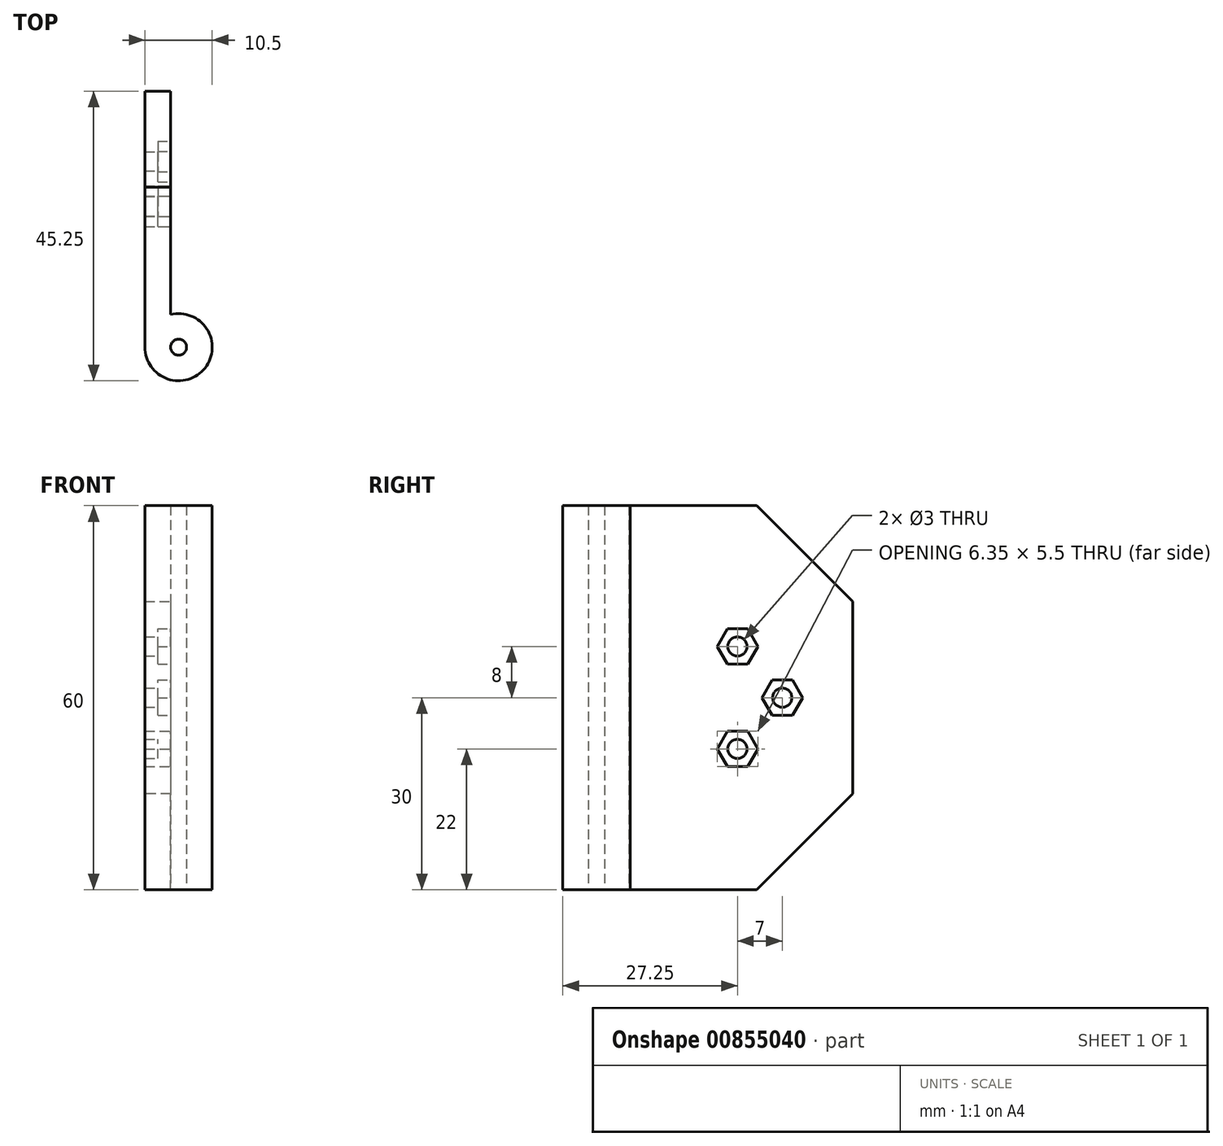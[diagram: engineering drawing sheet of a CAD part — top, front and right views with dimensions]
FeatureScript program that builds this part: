
annotation { "Feature Type Name" : "Feature", "Feature Type Description" : "" }
export const myFeature = defineFeature(function(context is Context, id is Id, definition is map)
    precondition{}
    {
        {
            var Q0;
            Q0=qCreatedBy(makeId("Top.planeOp"),FACE);
            var sketch = newSketch(context, id + "F0", { "sketchPlane" : qUnion([Q0])});
            skCircle(sketch, "E0", {"center": v(0, 0) * mm, "radius": 1.25 * mm});
            skCircle(sketch, "E1.0", {"center": v(0, 0) * mm, "radius": 5.25 * mm});
            skLineSegment(sketch, "E2", {"start": v(-5.25, 0) * mm, "end": v(-5.25, 40) * mm});
            skLineSegment(sketch, "E3", {"start": v(-5.25, 40) * mm, "end": v(-1.25, 40) * mm});
            skLineSegment(sketch, "E4", {"start": v(-1.25, 40) * mm, "end": v(-1.25, 0) * mm});
            skSolve(sketch);
        }
        {
            var Q0;
            {var subQ0=sQuery(id+"F0.wireOp",EDGE,"E2");Q0=makeQuery(id+"F0.imprint","IMPRINT",FACE,{"disambiguationData":[TD([[makeQuery(id+"F0.imprint","IMPRINT",EDGE,{"derivedFrom":subQ0}),-1.0]])]});}
            var Q1;
            Q1=makeQuery(id+"F0.imprint","IMPRINT",FACE,{"disambiguationData":[TD([[makeQuery(id+"F0.imprint","IMPRINT",EDGE,{"derivedFrom":sQuery(id+"F0.wireOp",EDGE,"E0")}),-1.0]])]});
            extrude(context, id + "F1", {"entities" : qUnion([Q0, Q1]), "endBound" : BoundingType.SYMMETRIC, "depth" : 60 * mm, "offsetDistance" : 25 * mm});
        }
        {
            var Q0;
            Q0=makeQuery(id+"F1.opExtrude","SWEPT_FACE",FACE,{"disambiguationData":[OSD([sQuery(id+"F0.wireOp",EDGE,"E4")])]});
            var sketch = newSketch(context, id + "F2", { "sketchPlane" : qUnion([Q0])});
            skLineSegment(sketch, "E5", {"start": v(0, 0) * mm, "end": v(29, 0) * mm, "construction": true});
            skLineSegment(sketch, "E6", {"start": v(22, 0) * mm, "end": v(22, 8) * mm, "construction": true});
            skPoint(sketch, "E7", {"position": v(22, 0) * mm});
            skCircle(sketch, "E8", {"center": v(22, 8) * mm, "radius": 1.5 * mm});
            skCircle(sketch, "E9", {"center": v(29, 0) * mm, "radius": 1.5 * mm});
            skCircle(sketch, "E10.MirrorC", {"center": v(22, -8) * mm, "radius": 1.5 * mm});
            skCircle(sketch, "E11.cCircle", {"center": v(22, 8) * mm, "radius": 2.75 * mm, "construction": true});
            skLineSegment(sketch, "E11.0", {"start": v(20.41, 10.75) * mm, "end": v(23.59, 10.75) * mm});
            skLineSegment(sketch, "E11.1", {"start": v(23.59, 10.75) * mm, "end": v(25.18, 8) * mm});
            skLineSegment(sketch, "E11.2", {"start": v(25.18, 8) * mm, "end": v(23.59, 5.25) * mm});
            skLineSegment(sketch, "E11.3", {"start": v(23.59, 5.25) * mm, "end": v(20.41, 5.25) * mm});
            skLineSegment(sketch, "E11.4", {"start": v(20.41, 5.25) * mm, "end": v(18.82, 8) * mm});
            skLineSegment(sketch, "E11.5", {"start": v(18.82, 8) * mm, "end": v(20.41, 10.75) * mm});
            skPoint(sketch, "E11.0.midPoint", {"position": v(22, 10.75) * mm});
            skCircle(sketch, "E12.MirrorC", {"center": v(22, -8) * mm, "radius": 2.75 * mm, "construction": true});
            skLineSegment(sketch, "E13.MirrorCS", {"start": v(20.41, -5.25) * mm, "end": v(18.82, -8) * mm});
            skLineSegment(sketch, "E14.MirrorCS", {"start": v(23.59, -5.25) * mm, "end": v(20.41, -5.25) * mm});
            skLineSegment(sketch, "E15.MirrorCS", {"start": v(25.18, -8) * mm, "end": v(23.59, -5.25) * mm});
            skLineSegment(sketch, "E16.MirrorCS", {"start": v(23.59, -10.75) * mm, "end": v(25.18, -8) * mm});
            skLineSegment(sketch, "E17.MirrorCS", {"start": v(20.41, -10.75) * mm, "end": v(23.59, -10.75) * mm});
            skLineSegment(sketch, "E18.MirrorCS", {"start": v(18.82, -8) * mm, "end": v(20.41, -10.75) * mm});
            skCircle(sketch, "E19.cCircle", {"center": v(29, 0) * mm, "radius": 2.75 * mm, "construction": true});
            skLineSegment(sketch, "E19.0", {"start": v(27.41, 2.75) * mm, "end": v(30.59, 2.75) * mm});
            skLineSegment(sketch, "E19.1", {"start": v(30.59, 2.75) * mm, "end": v(32.18, 0) * mm});
            skLineSegment(sketch, "E19.2", {"start": v(32.18, 0) * mm, "end": v(30.59, -2.75) * mm});
            skLineSegment(sketch, "E19.3", {"start": v(30.59, -2.75) * mm, "end": v(27.41, -2.75) * mm});
            skLineSegment(sketch, "E19.4", {"start": v(27.41, -2.75) * mm, "end": v(25.82, 0) * mm});
            skLineSegment(sketch, "E19.5", {"start": v(25.82, 0) * mm, "end": v(27.41, 2.75) * mm});
            skPoint(sketch, "E19.0.midPoint", {"position": v(29, 2.75) * mm});
            skSolve(sketch);
        }
        {
            var Q0;
            Q0=makeQuery(id+"F2.imprint","IMPRINT",FACE,{"disambiguationData":[TD([[makeQuery(id+"F2.imprint","IMPRINT",EDGE,{"derivedFrom":sQuery(id+"F2.wireOp",EDGE,"E8")}),1.0]])]});
            var Q1;
            Q1=makeQuery(id+"F2.imprint","IMPRINT",FACE,{"disambiguationData":[TD([[makeQuery(id+"F2.imprint","IMPRINT",EDGE,{"derivedFrom":sQuery(id+"F2.wireOp",EDGE,"E9")}),1.0]])]});
            var Q2;
            Q2=makeQuery(id+"F2.imprint","IMPRINT",FACE,{"disambiguationData":[TD([[makeQuery(id+"F2.imprint","IMPRINT",EDGE,{"derivedFrom":sQuery(id+"F2.wireOp",EDGE,"E10.MirrorC")}),-1.0]])]});
            extrude(context, id + "F3", {"entities" : qUnion([Q0, Q1, Q2]), "operationType" : NewBodyOperationType.REMOVE, "endBound" : BoundingType.THROUGH_ALL, "oppositeDirection" : true, "depth" : 25 * mm, "offsetDistance" : 25 * mm});
        }
        {
            var Q0;
            Q0=makeQuery(id+"F1.opExtrude","CAP_EDGE",EDGE,{"disambiguationData":[OSD([sQuery(id+"F0.wireOp",EDGE,"E3")])],"isStart":false});
            var Q1;
            Q1=makeQuery(id+"F1.opExtrude","CAP_EDGE",EDGE,{"disambiguationData":[OSD([sQuery(id+"F0.wireOp",EDGE,"E3")])],"isStart":true});
            chamfer(context, id + "F4", {"entities" : qUnion([Q0, Q1]), "width" : 15 * mm, "tangentPropagation" : true});
        }
        {
            var Q0;
            Q0=makeQuery(id+"F2.imprint","IMPRINT",FACE,{"disambiguationData":[TD([[makeQuery(id+"F2.imprint","IMPRINT",EDGE,{"derivedFrom":sQuery(id+"F2.wireOp",EDGE,"E8")}),-1.0]])]});
            var Q1;
            Q1=makeQuery(id+"F2.imprint","IMPRINT",FACE,{"disambiguationData":[TD([[makeQuery(id+"F2.imprint","IMPRINT",EDGE,{"derivedFrom":sQuery(id+"F2.wireOp",EDGE,"E9")}),-1.0]])]});
            var Q2;
            Q2=makeQuery(id+"F2.imprint","IMPRINT",FACE,{"disambiguationData":[TD([[makeQuery(id+"F2.imprint","IMPRINT",EDGE,{"derivedFrom":sQuery(id+"F2.wireOp",EDGE,"E10.MirrorC")}),1.0]])]});
            extrude(context, id + "F5", {"entities" : qUnion([Q0, Q1, Q2]), "operationType" : NewBodyOperationType.REMOVE, "oppositeDirection" : true, "depth" : 2 * mm, "offsetDistance" : 25 * mm});
        }
    });
